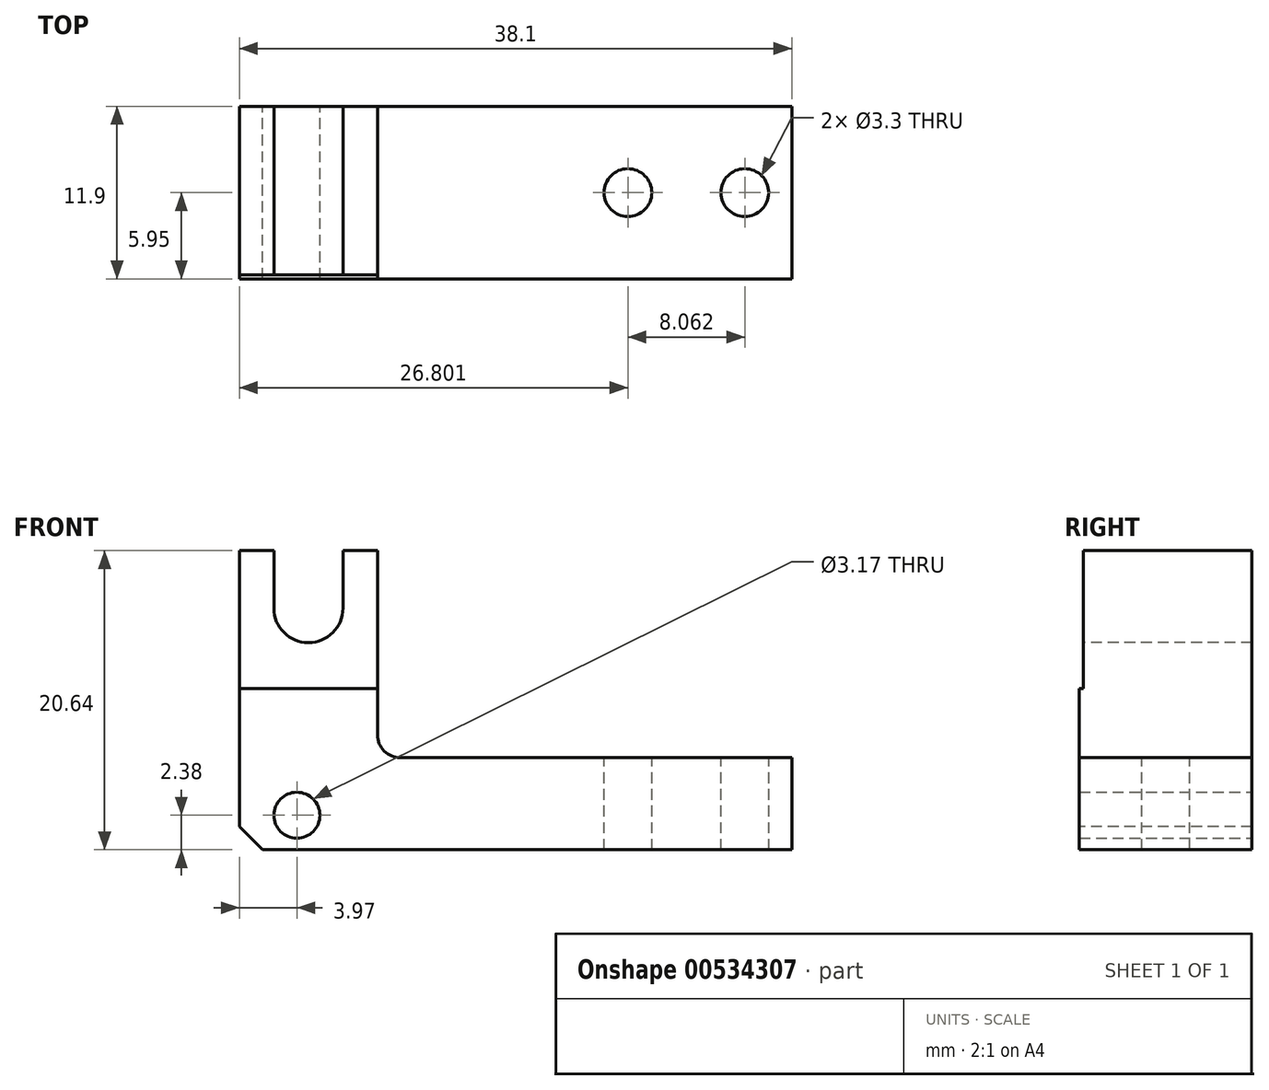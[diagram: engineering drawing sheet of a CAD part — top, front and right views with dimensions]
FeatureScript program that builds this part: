
annotation { "Feature Type Name" : "Feature", "Feature Type Description" : "" }
export const myFeature = defineFeature(function(context is Context, id is Id, definition is map)
    precondition{}
    {
        {
            var Q0;
            Q0=qCreatedBy(makeId("Front.planeOp"),FACE);
            var sketch = newSketch(context, id + "F0", { "sketchPlane" : qUnion([Q0])});
            skCircle(sketch, "E0", {"center": v(0, 0) * mm, "radius": 1.59 * mm});
            skLineSegment(sketch, "E1", {"start": v(-3.97, 18.26) * mm, "end": v(-3.97, -2.38) * mm});
            skLineSegment(sketch, "E2", {"start": v(-3.97, -2.38) * mm, "end": v(34.13, -2.38) * mm});
            skLineSegment(sketch, "E3", {"start": v(34.13, -2.38) * mm, "end": v(34.13, 3.97) * mm});
            skLineSegment(sketch, "E4", {"start": v(34.13, 3.97) * mm, "end": v(7.14, 3.97) * mm});
            skLineSegment(sketch, "E5", {"start": v(5.56, 5.56) * mm, "end": v(5.56, 18.26) * mm});
            skLineSegment(sketch, "E6", {"start": v(5.56, 18.26) * mm, "end": v(-3.97, 18.26) * mm});
            skPoint(sketch, "E7.visualSharp", {"position": v(5.56, 3.97) * mm});
            skArc(sketch, "E7.filletArc", {"start": v(5.56, 5.56) * mm, "mid": v(6.02, 4.43) * mm, "end": v(7.14, 3.97) * mm});
            skSolve(sketch);
        }
        {
            var Q0;
            Q0 = qSketchRegion(id + "F0", true);
            extrude(context, id + "F1", {"entities" : qUnion([Q0]), "endBound" : BoundingType.SYMMETRIC, "depth" : 11.9 * mm, "offsetDistance" : 25.4 * mm});
        }
        {
            var Q0;
            Q0=makeQuery(id+"F1.opExtrude","SWEPT_EDGE",EDGE,{"disambiguationData":[OSD([sQuery(id+"F0.wireOp",EDGE,"E1"),sQuery(id+"F0.wireOp",EDGE,"E2")])]});
            chamfer(context, id + "F2", {"entities" : qUnion([Q0]), "width" : 1.59 * mm, "tangentPropagation" : true});
        }
        {
            var Q0;
            Q0=makeQuery(id+"F1.opExtrude","CAP_FACE",FACE,{"disambiguationData":[OSD([sQuery(id+"F0.wireOp",EDGE,"E0"),sQuery(id+"F0.wireOp",EDGE,"E1"),sQuery(id+"F0.wireOp",EDGE,"E2"),sQuery(id+"F0.wireOp",EDGE,"E3"),sQuery(id+"F0.wireOp",EDGE,"E4"),sQuery(id+"F0.wireOp",EDGE,"E5"),sQuery(id+"F0.wireOp",EDGE,"E6"),sQuery(id+"F0.wireOp",EDGE,"E7.filletArc")])],"isStart":false});
            var sketch = newSketch(context, id + "F3", { "sketchPlane" : qUnion([Q0])});
            skLineSegment(sketch, "E8.bottom", {"start": v(-3.97, 18.26) * mm, "end": v(5.56, 18.26) * mm});
            skLineSegment(sketch, "E8.top", {"start": v(-3.97, 8.73) * mm, "end": v(5.56, 8.73) * mm});
            skLineSegment(sketch, "E8.left", {"start": v(-3.97, 18.26) * mm, "end": v(-3.97, 8.73) * mm});
            skLineSegment(sketch, "E8.right", {"start": v(5.56, 18.26) * mm, "end": v(5.56, 8.73) * mm});
            skSolve(sketch);
        }
        {
            var Q0;
            Q0 = qSketchRegion(id + "F3", true);
            extrude(context, id + "F4", {"entities" : qUnion([Q0]), "operationType" : NewBodyOperationType.REMOVE, "oppositeDirection" : true, "depth" : (.25 + (1 / 32)) * mm, "offsetDistance" : 25.4 * mm});
        }
        {
            var Q0;
            Q0=makeQuery(id+"F4.boolean.opBoolean","COPY",FACE,{"derivedFrom":makeQuery(id+"F4.opExtrude","CAP_FACE",FACE,{"disambiguationData":[OSD([sQuery(id+"F3.wireOp",EDGE,"E8.bottom"),sQuery(id+"F3.wireOp",EDGE,"E8.top"),sQuery(id+"F3.wireOp",EDGE,"E8.left"),sQuery(id+"F3.wireOp",EDGE,"E8.right")])],"isStart":false})});
            var sketch = newSketch(context, id + "F5", { "sketchPlane" : qUnion([Q0])});
            skLineSegment(sketch, "E9.bottom", {"start": v(-1.59, 18.26) * mm, "end": v(3.18, 18.26) * mm});
            skLineSegment(sketch, "E9.left", {"start": v(-1.59, 18.26) * mm, "end": v(-1.59, 14.29) * mm});
            skLineSegment(sketch, "E9.right", {"start": v(3.17, 18.26) * mm, "end": v(3.18, 14.29) * mm});
            skArc(sketch, "E10", {"start": v(-1.59, 14.29) * mm, "mid": v(0.8, 11.9) * mm, "end": v(3.17, 14.29) * mm});
            skLineSegment(sketch, "E11", {"start": v(0.8, 11.9) * mm, "end": v(6.43, 11.9) * mm});
            skSolve(sketch);
        }
        {
            var Q0;
            Q0 = qSketchRegion(id + "F5", true);
            extrude(context, id + "F6", {"entities" : qUnion([Q0]), "operationType" : NewBodyOperationType.REMOVE, "endBound" : BoundingType.THROUGH_ALL, "oppositeDirection" : true, "depth" : 25.4 * mm, "offsetDistance" : 25.4 * mm});
        }
        {
            var Q0;
            Q0=makeQuery(id+"F1.opExtrude","SWEPT_FACE",FACE,{"disambiguationData":[OSD([sQuery(id+"F0.wireOp",EDGE,"E4")])]});
            var sketch = newSketch(context, id + "F7", { "sketchPlane" : qUnion([Q0])});
            skCircle(sketch, "E12", {"center": v(30.9, 0) * mm, "radius": 1.65 * mm});
            skCircle(sketch, "E13", {"center": v(22.83, 0) * mm, "radius": 1.65 * mm});
            skLineSegment(sketch, "E14", {"start": v(32.54, 0) * mm, "end": v(32.54, 1.08) * mm, "construction": true});
            skLineSegment(sketch, "E15", {"start": v(24.48, 0) * mm, "end": v(24.48, 2.09) * mm, "construction": true});
            skLineSegment(sketch, "E16", {"start": v(29.24, 0) * mm, "end": v(29.24, -4.38) * mm, "construction": true});
            skSolve(sketch);
        }
        {
            var Q0;
            Q0=makeQuery(id+"F7.imprint","IMPRINT",FACE,{"disambiguationData":[TD([[makeQuery(id+"F7.imprint","IMPRINT",EDGE,{"derivedFrom":sQuery(id+"F7.wireOp",EDGE,"E13")}),1.0]])]});
            var Q1;
            Q1=makeQuery(id+"F7.imprint","IMPRINT",FACE,{"disambiguationData":[TD([[makeQuery(id+"F7.imprint","IMPRINT",EDGE,{"derivedFrom":sQuery(id+"F7.wireOp",EDGE,"E12")}),1.0]])]});
            var Q2;
            Q2=sQuery(id+"F7.wireOp",EDGE,"E13");
            var Q3;
            Q3=sQuery(id+"F7.wireOp",EDGE,"E12");
            extrude(context, id + "F8", {"entities" : qUnion([Q0, Q1]), "operationType" : NewBodyOperationType.REMOVE, "surfaceEntities" : qUnion([Q2, Q3]), "endBound" : BoundingType.THROUGH_ALL, "oppositeDirection" : true, "depth" : 25.4 * mm, "offsetDistance" : 25.4 * mm});
        }
    });
